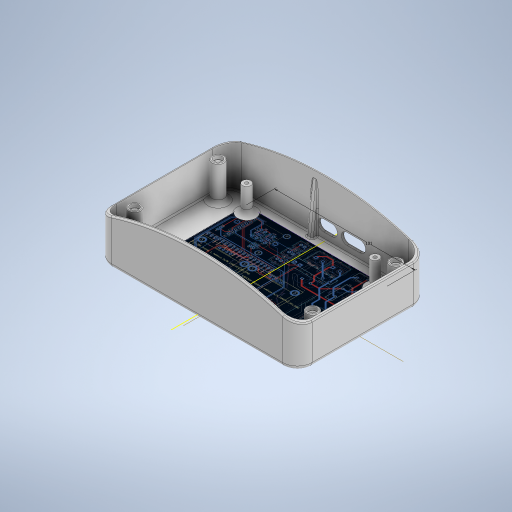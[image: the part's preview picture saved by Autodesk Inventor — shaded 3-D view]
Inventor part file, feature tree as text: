
AUTODESK INVENTOR PART (.ipt)
format: ipt  version: 2024 (Build 280153000, 153)  size: 966,656 bytes
history: native  units: mm
features: sketch x14, extrude x12, fillet x11, projected_geometry x5, mirror x2, other x2, plane x1
ambient origin geometry x8: Origin, YZ Plane, XZ Plane, XY Plane, X Axis, Y Axis, Z Axis, Center Point
bodies: Solid1 (feature_tree)
feature tree (47):
  extrude  "Extrusion1"  Depth=93.65mm
  extrude  "Extrusion2"  Depth=140.55mm
  fillet  "Fillet1"  Radius=90.25mm
  extrude  "Extrusion3"  Depth=10.5mm
  fillet  "Fillet2"  Radius=13.3mm
  fillet  "Fillet3"  Radius=50.0mm
  fillet  "Fillet4"  Radius=3.0mm
  extrude  "Extrusion4"  Depth=1.0mm
  extrude  "Extrusion5"  Depth=25.542mm TaperAngle=0.0deg
  extrude  "Extrusion6"  Depth=5.0mm TaperAngle=0.0deg
  mirror  "Mirror1"
  fillet  "Fillet5"  Radius=6.0mm
  fillet  "Fillet6"  Radius=2.57mm
  plane  "Work Plane1"
  mirror  "Mirror3"
  sketch  "Sketch9"  dims[d26=8.2mm d27=3.0mm]
  sketch  "Sketch10"  dims[d28=1.0mm d29=42.0mm d31=27.341709mm]
  fillet  "Fillet7"  Radius=14.8mm
  extrude  "Extrusion9"  Depth=3.0mm
  extrude  "Extrusion10"  Depth=42.0mm
  other  "screws"
  fillet  "Fillet10"  Radius=27.341709mm
  extrude  "Extrusion11"  Depth=0.5mm
  fillet  "Fillet11"  Radius=101.0mm
  extrude  "Extrusion12"  Depth=18.5mm TaperAngle=0.0deg
  extrude  "Extrusion13"  Depth=10.0mm TaperAngle=0.0deg
  fillet  "Fillet12"  [1 undecoded]
  extrude  "Extrusion14"  Depth=6.0mm
  fillet  "Fillet13"  Radius=2.4mm
  sketch  "Sketch1"  dims[d0=143.95mm d1=93.65mm]
  sketch  "Sketch2"  dims[d2=2.0mm d3=0.0mm d4=140.55mm d5=90.25mm]
  sketch  "Sketch3"  dims[d6=40.0mm d7=0.0mm d8=10.5mm d9=13.3mm d10=50.0mm d11=0.0mm d12=3.0mm]
  sketch  "Sketch5"  dims[d13=1.0mm d14=1.0mm]
  sketch  "Sketch6"  dims[d15=8.5mm d17=25.542mm d18=0.0mm]
  sketch  "Sketch7"  dims[d19=3.47mm d20=5.0mm d21=0.0mm d22=6.0mm d23=2.57mm d24=0.0mm d25=14.8mm]
  other  "Image4"
  sketch  "Sketch14"  dims[d33=-2.1mm d68=0.5mm d123=101.0mm]
  sketch  "Sketch15"  dims[d129=6.0mm d130=18.5mm d131=0.0mm]
  projected_geometry  "Projected Loop1"
  projected_geometry  "Projected Loop2"
  projected_geometry  "Projected Loop3"
  sketch  "Sketch16"  dims[d132=2.4mm d133=10.0mm d134=0.0mm d136=-7.75mm]
  sketch  "Sketch17"  dims[d137=6.0mm d138=6.0mm d139=2.4mm]
  sketch  "Sketch18"  dims[d140=2.4mm]
  projected_geometry  "Projected Loop4"
  projected_geometry  "Projected Loop5"
  sketch  "Sketch19"  dims[d141=2.4mm d142=4.0mm d143=4.0mm d144=43.0mm d145=34.0mm d146=8.0mm d147=18.5mm d148=0.0mm d149=4.0mm d150=4.0mm d151=4.0mm d152=35.0mm d153=0.0mm d154=35.0mm d155=0.0mm d156=1.0mm d157=3.0mm d158=0.0mm d159=0.0mm d160=4.0mm]
note: 1 required parameter value undecoded (feature->parameter linkage not recoverable at this tier; creation-order binding heuristic only, values carry confidence <= 0.55)
